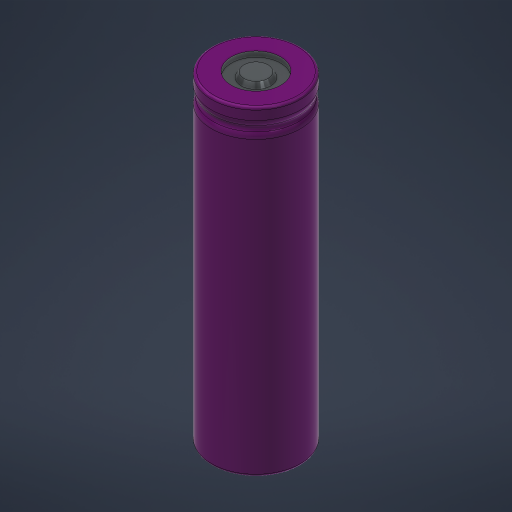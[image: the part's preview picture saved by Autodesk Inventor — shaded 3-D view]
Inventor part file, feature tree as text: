
AUTODESK INVENTOR PART (.ipt)
format: ipt  version: 2024.3 (Build 283343010, 343A)  size: 215,552 bytes
history: native  units: mm
features: revolve x1, fillet x1, sketch x1
ambient origin geometry x8: Origin, YZ Plane, XZ Plane, XY Plane, X Axis, Y Axis, Z Axis, Center Point
bodies: Body1 (feature_tree)
feature tree (3):
  revolve  "Umdrehung1"
  fillet  "Rundung1"  Radius=18.0mm
  sketch  "Skizze1"  dims[d5=1.0mm d6=19.0mm d7=0.5mm d8=0.1mm d9=14.0mm d10=1.0mm d11=10.0mm d12=6.0mm d13=4.0mm d14=60.0deg d15=90.0deg d16=2.0mm d17=0.1mm d18=65.0mm]
